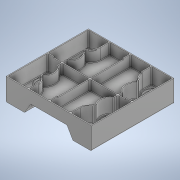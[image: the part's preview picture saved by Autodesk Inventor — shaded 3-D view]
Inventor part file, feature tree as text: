
AUTODESK INVENTOR PART (.ipt)
format: ipt  version: 2021 (Build 250183000, 183)  size: 744,960 bytes
history: native  units: mm
features: extrude x5, fillet x3, sketch x2, mirror x2, projected_geometry x2, chamfer x1, pattern_circular x1
ambient origin geometry x8: Origin, YZ Plane, XZ Plane, XY Plane, X Axis, Y Axis, Z Axis, Center Point
bodies: Solid1 (feature_tree)
feature tree (16):
  sketch  "Sketch1"  dims[d0=74.0mm d2=38.0mm d3=108.4mm]
  extrude  "Extrusion1"  Depth=38.0mm
  fillet  "Fillet1"  Radius=108.4mm
  sketch  "Sketch2"  dims[d4=0.5mm d5=0.25mm d6=91.0mm d7=142.25mm d8=0.0mm d9=2.0mm d10=32.0mm d13=23.0mm d23=0.4mm d24=37.0mm d25=0.0mm d26=23.5mm d27=33.0mm d28=2.0mm d47=27.0mm d48=0.0mm d49=2.0mm d50=2.0mm d51=45.0deg d53=20.1mm d70=4.976467mm d71=7.689824mm d72=101.0mm d73=97.275208mm d74=24.545793mm d75=8.0mm d76=12.062433mm d77=5.447284mm d78=1.6mm d79=1.6mm d80=0.8mm d81=20.5mm d82=1.0mm d83=5.0mm d84=0.5mm d85=0.5mm d86=0.5mm d87=2.0mm d88=0.0mm d103=60.0mm d104=360.0deg d106=25.0mm d107=9.0mm d108=2.0mm d109=3.0mm d110=0.8mm d111=19.1mm d112=0.0mm d115=4.0mm d116=1.0mm d121=20.0mm d122=1.0mm]
  extrude  "Extrusion2"  Depth=1.0mm
  extrude  "Extrusion3"  Depth=1.0mm
  chamfer  "Chamfer1"  Distance=142.25mm
  fillet  "Fillet3"  [1 undecoded]
  extrude  "Extrusion8"  Depth=2.0mm
  fillet  "Fillet4"  Radius=32.0mm
  mirror  "Mirror1"
  mirror  "Mirror2"
  extrude  "Extrusion6"  Depth=1.0mm
  pattern_circular  "Circular Pattern1"  [2 undecoded]
  projected_geometry  "Projected Loop1"
  projected_geometry  "Projected Loop7"
note: 3 required parameter values undecoded (feature->parameter linkage not recoverable at this tier; creation-order binding heuristic only, values carry confidence <= 0.55)
